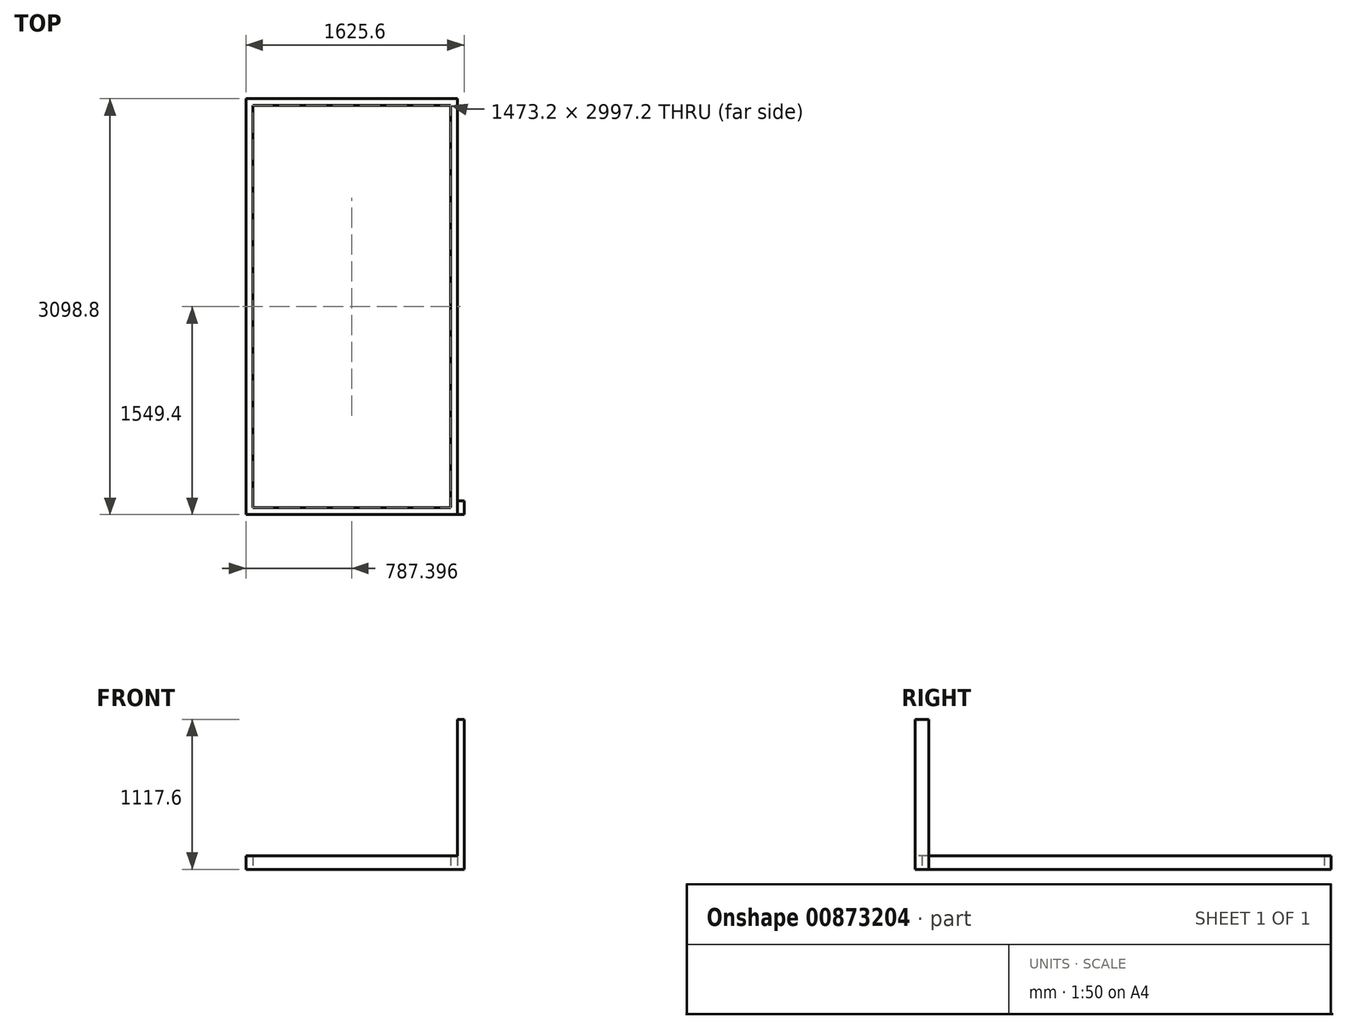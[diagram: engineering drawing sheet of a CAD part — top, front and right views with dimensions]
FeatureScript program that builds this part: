
annotation { "Feature Type Name" : "Feature", "Feature Type Description" : "" }
export const myFeature = defineFeature(function(context is Context, id is Id, definition is map)
    precondition{}
    {
        {
            var Q0;
            Q0=qCreatedBy(makeId("Front.planeOp"),FACE);
            var sketch = newSketch(context, id + "F0", { "sketchPlane" : qUnion([Q0])});
            skLineSegment(sketch, "E0.bottom", {"start": v(-460.4, 101.6) * mm, "end": v(-409.6, 101.6) * mm});
            skLineSegment(sketch, "E0.top", {"start": v(-460.4, 0) * mm, "end": v(-409.6, 0) * mm});
            skLineSegment(sketch, "E0.left", {"start": v(-460.4, 101.6) * mm, "end": v(-460.4, 0) * mm});
            skLineSegment(sketch, "E0.right", {"start": v(-409.6, 101.6) * mm, "end": v(-409.6, 0) * mm});
            skSolve(sketch);
        }
        {
            var Q0;
            Q0=makeQuery(id+"F0.imprint","IMPRINT",FACE,{"disambiguationData":[TD([[makeQuery(id+"F0.imprint","IMPRINT",EDGE,{"derivedFrom":sQuery(id+"F0.wireOp",EDGE,"E0.bottom")}),-1.0]])]});
            extrude(context, id + "F1", {"entities" : qUnion([Q0]), "depth" : 3048 * mm, "offsetDistance" : 25.4 * mm});
        }
        {
            var Q0;
            Q0=makeQuery(id+"F1.opExtrude","SWEPT_FACE",FACE,{"disambiguationData":[OSD([sQuery(id+"F0.wireOp",EDGE,"E0.right")])]});
            var sketch = newSketch(context, id + "F2", { "sketchPlane" : qUnion([Q0])});
            skLineSegment(sketch, "E1.bottom", {"start": v(-3048, 101.6) * mm, "end": v(-2997.2, 101.6) * mm});
            skLineSegment(sketch, "E1.top", {"start": v(-3048, 0) * mm, "end": v(-2997.2, 0) * mm});
            skLineSegment(sketch, "E1.left", {"start": v(-3048, 101.6) * mm, "end": v(-3048, 0) * mm});
            skLineSegment(sketch, "E1.right", {"start": v(-2997.2, 101.6) * mm, "end": v(-2997.2, 0) * mm});
            skSolve(sketch);
        }
        {
            var Q0;
            Q0=makeQuery(id+"F2.imprint","IMPRINT",FACE,{"disambiguationData":[TD([[makeQuery(id+"F2.imprint","IMPRINT",EDGE,{"derivedFrom":sQuery(id+"F2.wireOp",EDGE,"E1.bottom")}),-1.0]])]});
            extrude(context, id + "F3", {"entities" : qUnion([Q0]), "operationType" : NewBodyOperationType.ADD, "depth" : 1524 * mm, "offsetDistance" : 25.4 * mm});
        }
        {
            var Q0;
            Q0=makeQuery(id+"F3.opExtrude","SWEPT_FACE",FACE,{"disambiguationData":[OSD([sQuery(id+"F2.wireOp",EDGE,"E1.right")])]});
            var sketch = newSketch(context, id + "F4", { "sketchPlane" : qUnion([Q0])});
            skLineSegment(sketch, "E2.bottom", {"start": v(-1114.4, 101.6) * mm, "end": v(-1063.6, 101.6) * mm});
            skLineSegment(sketch, "E2.top", {"start": v(-1114.4, 0) * mm, "end": v(-1063.6, 0) * mm});
            skLineSegment(sketch, "E2.left", {"start": v(-1114.4, 101.6) * mm, "end": v(-1114.4, 0) * mm});
            skLineSegment(sketch, "E2.right", {"start": v(-1063.6, 101.6) * mm, "end": v(-1063.6, 0) * mm});
            skSolve(sketch);
        }
        {
            var Q0;
            Q0=makeQuery(id+"F4.imprint","IMPRINT",FACE,{"disambiguationData":[TD([[makeQuery(id+"F4.imprint","IMPRINT",EDGE,{"derivedFrom":sQuery(id+"F4.wireOp",EDGE,"E2.bottom")}),-1.0]])]});
            extrude(context, id + "F5", {"entities" : qUnion([Q0]), "operationType" : NewBodyOperationType.ADD, "depth" : 3048 * mm, "offsetDistance" : 25.4 * mm});
        }
        {
            var Q0;
            Q0=makeQuery(id+"F5.opExtrude","SWEPT_FACE",FACE,{"disambiguationData":[OSD([sQuery(id+"F4.wireOp",EDGE,"E2.right")])]});
            var sketch = newSketch(context, id + "F6", { "sketchPlane" : qUnion([Q0])});
            skLineSegment(sketch, "E3.bottom", {"start": v(-50.8, 101.6) * mm, "end": v(0, 101.6) * mm});
            skLineSegment(sketch, "E3.top", {"start": v(-50.8, 0) * mm, "end": v(0, 0) * mm});
            skLineSegment(sketch, "E3.left", {"start": v(-50.8, 101.6) * mm, "end": v(-50.8, 0) * mm});
            skLineSegment(sketch, "E3.right", {"start": v(0, 101.6) * mm, "end": v(0, 0) * mm});
            skSolve(sketch);
        }
        {
            var Q0;
            Q0=makeQuery(id+"F6.imprint","IMPRINT",FACE,{"disambiguationData":[TD([[makeQuery(id+"F6.imprint","IMPRINT",EDGE,{"derivedFrom":sQuery(id+"F6.wireOp",EDGE,"E3.bottom")}),-1.0]])]});
            extrude(context, id + "F7", {"entities" : qUnion([Q0]), "operationType" : NewBodyOperationType.ADD, "depth" : 1524 * mm, "offsetDistance" : 25.4 * mm});
        }
        {
            var Q0;
            Q0=makeQuery(id+"F5.boolean.opBoolean","MERGE",FACE,{"derivedFrom":[makeQuery(id+"F3.opExtrude","CAP_FACE",FACE,{"disambiguationData":[OSD([sQuery(id+"F2.wireOp",EDGE,"E1.bottom"),sQuery(id+"F2.wireOp",EDGE,"E1.top"),sQuery(id+"F2.wireOp",EDGE,"E1.left"),sQuery(id+"F2.wireOp",EDGE,"E1.right")])],"isStart":false}),makeQuery(id+"F5.opExtrude","SWEPT_FACE",FACE,{"disambiguationData":[OSD([sQuery(id+"F4.wireOp",EDGE,"E2.left")])]})]});
            var sketch = newSketch(context, id + "F8", { "sketchPlane" : qUnion([Q0])});
            skLineSegment(sketch, "E4.bottom", {"start": v(-3048, 101.6) * mm, "end": v(-2946.4, 101.6) * mm});
            skLineSegment(sketch, "E4.top", {"start": v(-3048, 0) * mm, "end": v(-2946.4, 0) * mm});
            skLineSegment(sketch, "E4.left", {"start": v(-3048, 101.6) * mm, "end": v(-3048, 0) * mm});
            skLineSegment(sketch, "E4.right", {"start": v(-2946.4, 101.6) * mm, "end": v(-2946.4, 0) * mm});
            skSolve(sketch);
        }
        {
            var Q0;
            Q0=makeQuery(id+"F8.imprint","IMPRINT",FACE,{"disambiguationData":[TD([[makeQuery(id+"F8.imprint","IMPRINT",EDGE,{"derivedFrom":sQuery(id+"F8.wireOp",EDGE,"E4.bottom")}),-1.0]])]});
            extrude(context, id + "F9", {"entities" : qUnion([Q0]), "operationType" : NewBodyOperationType.ADD, "depth" : 50.8 * mm, "offsetDistance" : 25.4 * mm});
        }
        {
            var Q0;
            Q0=makeQuery(id+"F9.boolean.opBoolean","MERGE",FACE,{"derivedFrom":[makeQuery(id+"F7.boolean.opBoolean","MERGE",FACE,{"derivedFrom":[makeQuery(id+"F5.boolean.opBoolean","MERGE",FACE,{"derivedFrom":[makeQuery(id+"F3.boolean.opBoolean","MERGE",FACE,{"derivedFrom":[makeQuery(id+"F1.opExtrude","SWEPT_FACE",FACE,{"disambiguationData":[OSD([sQuery(id+"F0.wireOp",EDGE,"E0.bottom")])]}),makeQuery(id+"F3.opExtrude","SWEPT_FACE",FACE,{"disambiguationData":[OSD([sQuery(id+"F2.wireOp",EDGE,"E1.bottom")])]})]}),makeQuery(id+"F5.opExtrude","SWEPT_FACE",FACE,{"disambiguationData":[OSD([sQuery(id+"F4.wireOp",EDGE,"E2.bottom")])]})]}),makeQuery(id+"F7.opExtrude","SWEPT_FACE",FACE,{"disambiguationData":[OSD([sQuery(id+"F6.wireOp",EDGE,"E3.bottom")])]})]}),makeQuery(id+"F9.opExtrude","SWEPT_FACE",FACE,{"disambiguationData":[OSD([sQuery(id+"F8.wireOp",EDGE,"E4.bottom")])]})]});
            var sketch = newSketch(context, id + "F10", { "sketchPlane" : qUnion([Q0])});
            skLineSegment(sketch, "E5.bottom", {"start": v(1165.2, -2946.4) * mm, "end": v(1114.4, -2946.4) * mm});
            skLineSegment(sketch, "E5.top", {"start": v(1165.2, -3048) * mm, "end": v(1114.4, -3048) * mm});
            skLineSegment(sketch, "E5.left", {"start": v(1165.2, -2946.4) * mm, "end": v(1165.2, -3048) * mm});
            skLineSegment(sketch, "E5.right", {"start": v(1114.4, -2946.4) * mm, "end": v(1114.4, -3048) * mm});
            skSolve(sketch);
        }
        {
            var Q0;
            Q0=makeQuery(id+"F10.imprint","IMPRINT",FACE,{"disambiguationData":[TD([[makeQuery(id+"F10.imprint","IMPRINT",EDGE,{"derivedFrom":sQuery(id+"F10.wireOp",EDGE,"E5.bottom")}),1.0]])]});
            extrude(context, id + "F11", {"entities" : qUnion([Q0]), "operationType" : NewBodyOperationType.ADD, "depth" : 1016 * mm, "offsetDistance" : 25.4 * mm});
        }
    });
